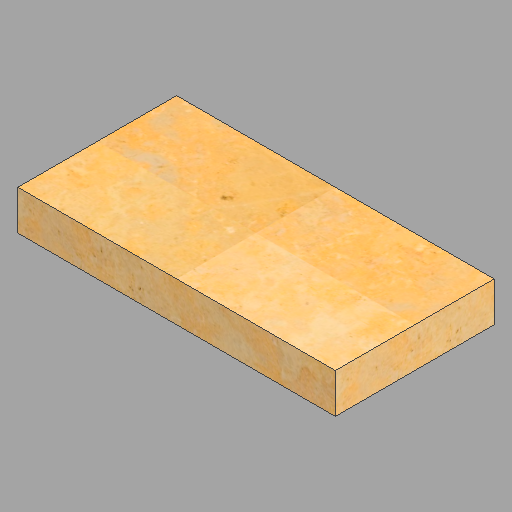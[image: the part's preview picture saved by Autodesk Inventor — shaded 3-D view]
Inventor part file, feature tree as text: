
AUTODESK INVENTOR PART (.ipt)
format: ipt  version: 2023 (Build 270158030, 158C)  size: 264,192 bytes
history: native  units: in
note: dims shown in document units (in); Inventor stores cm internally (conversion verified against a paired STEP export)
features: other x1, extrude x1, sketch x1
ambient origin geometry x8: Origin, YZ Plane, XZ Plane, XY Plane, X Axis, Y Axis, Z Axis, Center Point
bodies: Solid1 (feature_tree)
feature tree (3):
  other  "8X16X2 - 91"
  extrude  "Extrusion1"  Depth=8.0in
  sketch  "Sketch1"  dims[d0=16.0in d1=8.0in d2=2.0in d3=0.0in]
